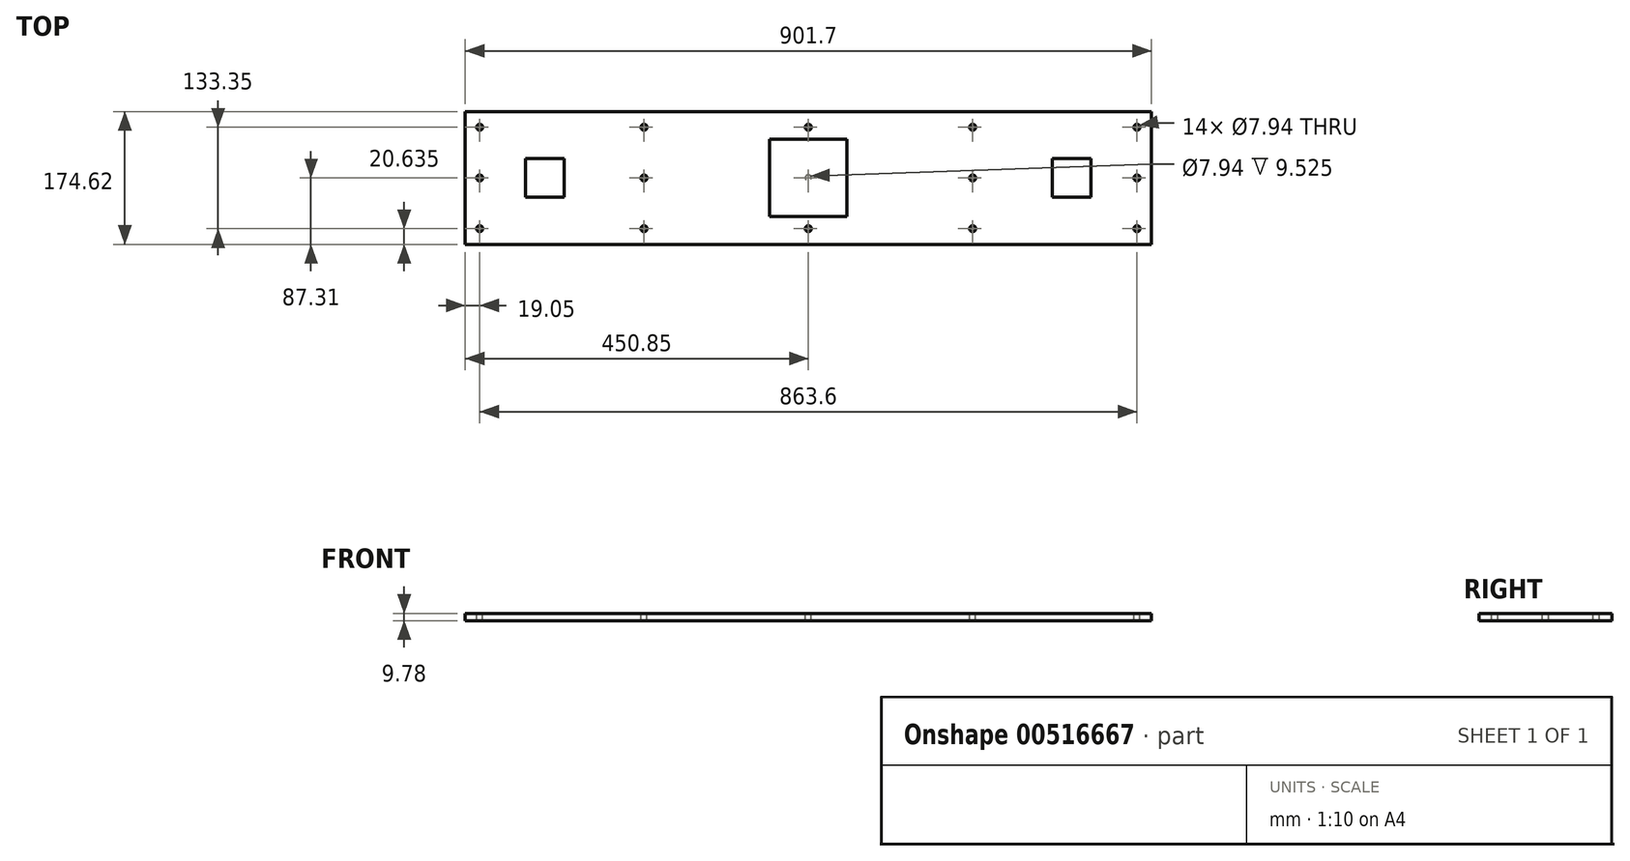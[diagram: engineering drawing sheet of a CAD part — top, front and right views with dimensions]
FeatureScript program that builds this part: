
annotation { "Feature Type Name" : "Feature", "Feature Type Description" : "" }
export const myFeature = defineFeature(function(context is Context, id is Id, definition is map)
    precondition{}
    {
        {
            var Q0;
            Q0=qCreatedBy(makeId("Top.planeOp"),FACE);
            var sketch = newSketch(context, id + "F0", { "sketchPlane" : qUnion([Q0])});
            skPoint(sketch, "E0.middle", {"position": v(0, 0) * mm});
            skLineSegment(sketch, "E1.bottom", {"start": v(450.85, 87.31) * mm, "end": v(-450.85, 87.31) * mm});
            skLineSegment(sketch, "E1.top", {"start": v(450.85, -87.31) * mm, "end": v(-450.85, -87.31) * mm});
            skLineSegment(sketch, "E1.left", {"start": v(450.85, 87.31) * mm, "end": v(450.85, -87.31) * mm});
            skLineSegment(sketch, "E1.right", {"start": v(-450.85, 87.31) * mm, "end": v(-450.85, -87.31) * mm});
            skSolve(sketch);
        }
        {
            var Q0;
            Q0=makeQuery(id+"F0.imprint","IMPRINT",FACE,{"disambiguationData":[TD([[makeQuery(id+"F0.imprint","IMPRINT",EDGE,{"derivedFrom":sQuery(id+"F0.wireOp",EDGE,"E1.bottom")}),1.0]])]});
            extrude(context, id + "F1", {"entities" : qUnion([Q0]), "endBound" : BoundingType.SYMMETRIC, "depth" : 9.52 * mm, "offsetDistance" : 25.4 * mm});
        }
        {
            var Q0;
            Q0=makeQuery(id+"F1.opExtrude","CAP_FACE",FACE,{"disambiguationData":[OSD([sQuery(id+"F0.wireOp",EDGE,"E1.bottom"),sQuery(id+"F0.wireOp",EDGE,"E1.top"),sQuery(id+"F0.wireOp",EDGE,"E1.left"),sQuery(id+"F0.wireOp",EDGE,"E1.right")])],"isStart":false});
            var sketch = newSketch(context, id + "F2", { "sketchPlane" : qUnion([Q0])});
            skPoint(sketch, "E2", {"position": v(-431.8, 66.67) * mm});
            skPoint(sketch, "E3", {"position": v(-431.8, 0) * mm});
            skPoint(sketch, "E4", {"position": v(-431.8, -66.68) * mm});
            skPoint(sketch, "E5", {"position": v(-215.9, -66.68) * mm});
            skPoint(sketch, "E6", {"position": v(-215.9, 0) * mm});
            skPoint(sketch, "E7", {"position": v(-215.9, 66.67) * mm});
            skPoint(sketch, "E8", {"position": v(0, 66.67) * mm});
            skPoint(sketch, "E9", {"position": v(0, 0) * mm});
            skPoint(sketch, "E10", {"position": v(0, -66.68) * mm});
            skPoint(sketch, "E11", {"position": v(215.9, -66.68) * mm});
            skPoint(sketch, "E12", {"position": v(215.9, 0) * mm});
            skPoint(sketch, "E13", {"position": v(215.9, 66.67) * mm});
            skPoint(sketch, "E14", {"position": v(431.8, 66.68) * mm});
            skPoint(sketch, "E15", {"position": v(431.8, 0) * mm});
            skPoint(sketch, "E16", {"position": v(431.8, -66.68) * mm});
            skSolve(sketch);
        }
        {
            var Q0;
            Q0=sQuery(id+"F2.wireOp",VERTEX,"E7");
            var Q1;
            Q1=sQuery(id+"F2.wireOp",VERTEX,"E6");
            var Q2;
            Q2=sQuery(id+"F2.wireOp",VERTEX,"E5");
            var Q3;
            Q3=sQuery(id+"F2.wireOp",VERTEX,"E2");
            var Q4;
            Q4=sQuery(id+"F2.wireOp",VERTEX,"E3");
            var Q5;
            Q5=sQuery(id+"F2.wireOp",VERTEX,"E4");
            var Q6;
            Q6=sQuery(id+"F2.wireOp",VERTEX,"E8");
            var Q7;
            Q7=sQuery(id+"F2.wireOp",VERTEX,"E9");
            var Q8;
            Q8=sQuery(id+"F2.wireOp",VERTEX,"E10");
            var Q9;
            Q9=sQuery(id+"F2.wireOp",VERTEX,"E13");
            var Q10;
            Q10=sQuery(id+"F2.wireOp",VERTEX,"E12");
            var Q11;
            Q11=sQuery(id+"F2.wireOp",VERTEX,"E11");
            var Q12;
            Q12=sQuery(id+"F2.wireOp",VERTEX,"E16");
            var Q13;
            Q13=sQuery(id+"F2.wireOp",VERTEX,"E15");
            var Q14;
            Q14=sQuery(id+"F2.wireOp",VERTEX,"E14");
            var Q15;
            Q15=makeQuery(id+"F1.opExtrude","SWEPT_BODY",BODY,{"disambiguationData":[OSD([sQuery(id+"F0.wireOp",EDGE,"E1.bottom"),sQuery(id+"F0.wireOp",EDGE,"E1.top"),sQuery(id+"F0.wireOp",EDGE,"E1.left"),sQuery(id+"F0.wireOp",EDGE,"E1.right")])]});
            hole(context, id + "F3", {"style" : HoleStyle.SIMPLE, "endStyle" : HoleEndStyle.THROUGH, "standardTappedOrClearance" : lookupTablePath({ "standard" : "ANSI", "engagement" : "75%", "pitch" : "16 tpi", "size" : "3/8", "type" : "Tapped" }), "standardBlindInLast" : lookupTablePath({ "standard" : "ANSI", "engagement" : "75%", "pitch" : "16 tpi", "size" : "3/8", "type" : "Tapped" }), "holeDiameter" : 7.94 * mm, "showTappedDepth" : true, "isTappedThrough" : true, "tappedDepth" : 12.7 * mm, "tapClearance" : 3, "locations" : qUnion([Q0, Q1, Q2, Q3, Q4, Q5, Q6, Q7, Q8, Q9, Q10, Q11, Q12, Q13, Q14]), "scope" : qUnion([Q15]), "majorDiameter" : 9.53 * mm});
        }
        {
            var Q0;
            Q0=makeQuery(id+"F1.opExtrude","CAP_FACE",FACE,{"disambiguationData":[OSD([sQuery(id+"F0.wireOp",EDGE,"E1.bottom"),sQuery(id+"F0.wireOp",EDGE,"E1.top"),sQuery(id+"F0.wireOp",EDGE,"E1.left"),sQuery(id+"F0.wireOp",EDGE,"E1.right")])],"isStart":false});
            var sketch = newSketch(context, id + "F4", { "sketchPlane" : qUnion([Q0])});
            skLineSegment(sketch, "E17.bottom", {"start": v(50.8, 50.8) * mm, "end": v(-50.8, 50.8) * mm});
            skLineSegment(sketch, "E17.top", {"start": v(50.8, -50.8) * mm, "end": v(-50.8, -50.8) * mm});
            skLineSegment(sketch, "E17.left", {"start": v(50.8, 50.8) * mm, "end": v(50.8, -50.8) * mm});
            skLineSegment(sketch, "E17.right", {"start": v(-50.8, 50.8) * mm, "end": v(-50.8, -50.8) * mm});
            skPoint(sketch, "E17.middle", {"position": v(0, 0) * mm});
            skLineSegment(sketch, "E18.bottom", {"start": v(-320.68, 25.4) * mm, "end": v(-371.48, 25.4) * mm});
            skLineSegment(sketch, "E18.top", {"start": v(-320.68, -25.4) * mm, "end": v(-371.48, -25.4) * mm});
            skLineSegment(sketch, "E18.left", {"start": v(-320.68, 25.4) * mm, "end": v(-320.68, -25.4) * mm});
            skLineSegment(sketch, "E18.right", {"start": v(-371.48, 25.4) * mm, "end": v(-371.48, -25.4) * mm});
            skPoint(sketch, "E18.middle", {"position": v(-346.08, 0) * mm});
            skLineSegment(sketch, "E19.bottom", {"start": v(371.48, 25.4) * mm, "end": v(320.68, 25.4) * mm});
            skLineSegment(sketch, "E19.top", {"start": v(371.48, -25.4) * mm, "end": v(320.68, -25.4) * mm});
            skLineSegment(sketch, "E19.left", {"start": v(371.48, 25.4) * mm, "end": v(371.48, -25.4) * mm});
            skLineSegment(sketch, "E19.right", {"start": v(320.68, 25.4) * mm, "end": v(320.68, -25.4) * mm});
            skPoint(sketch, "E19.middle", {"position": v(346.08, 0) * mm});
            skSolve(sketch);
        }
        {
            var Q0;
            Q0 = qSketchRegion(id + "F4", true);
            extrude(context, id + "F5", {"entities" : qUnion([Q0]), "operationType" : NewBodyOperationType.ADD, "depth" : 0.25 * mm, "offsetDistance" : 25.4 * mm});
        }
    });
